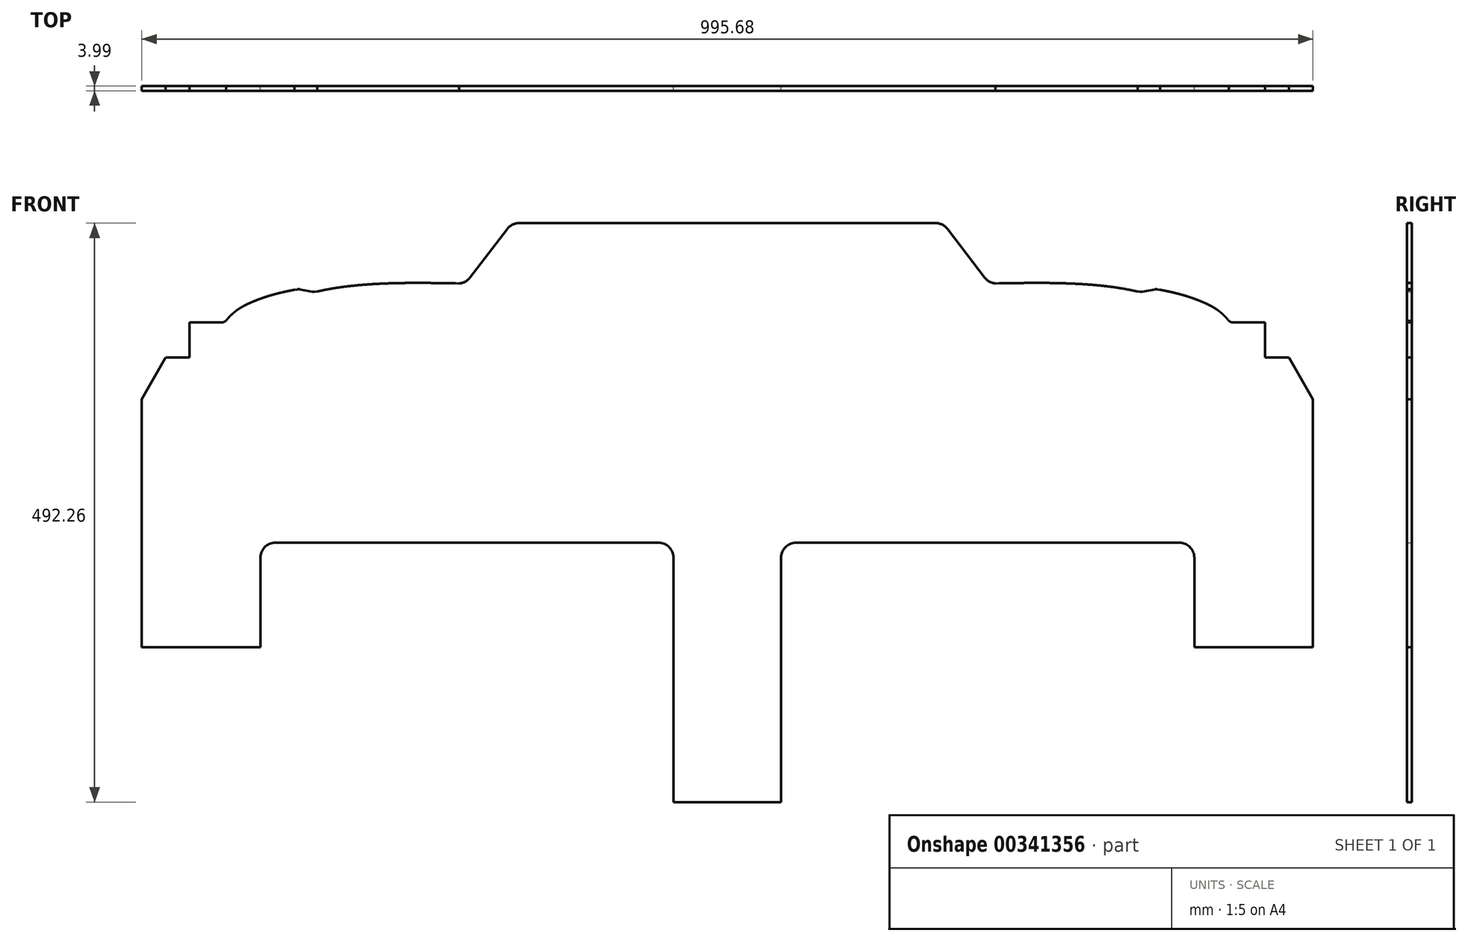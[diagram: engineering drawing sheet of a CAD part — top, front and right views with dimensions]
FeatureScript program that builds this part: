
annotation { "Feature Type Name" : "Feature", "Feature Type Description" : "" }
export const myFeature = defineFeature(function(context is Context, id is Id, definition is map)
    precondition{}
    {
        {
            var Q0;
            Q0=qCreatedBy(makeId("Front.planeOp"),FACE);
            var sketch = newSketch(context, id + "F0", { "sketchPlane" : qUnion([Q0])});
            skLineSegment(sketch, "E0", {"start": v(-497.84, 96.27) * mm, "end": v(-477.52, 131.83) * mm});
            skLineSegment(sketch, "E1", {"start": v(-477.52, 131.83) * mm, "end": v(-457.2, 131.83) * mm});
            skLineSegment(sketch, "E2", {"start": v(-457.2, 131.83) * mm, "end": v(-457.2, 161.67) * mm});
            skLineSegment(sketch, "E3", {"start": v(-457.2, 161.67) * mm, "end": v(-430.26, 161.67) * mm});
            skLineSegment(sketch, "E4", {"start": v(-187.2, 241.14) * mm, "end": v(-218.8, 199.83) * mm});
            skLineSegment(sketch, "E5", {"start": v(-367.96, 189.44) * mm, "end": v(-365.6, 189.83) * mm});
            skLineSegment(sketch, "E6", {"start": v(-363.38, 189.8) * mm, "end": v(-352.8, 187.74) * mm});
            skLineSegment(sketch, "E7", {"start": v(-350.76, 187.68) * mm, "end": v(-348.83, 187.94) * mm});
            skLineSegment(sketch, "E8", {"start": v(-397, -38.35) * mm, "end": v(-397, -114.55) * mm});
            skLineSegment(sketch, "E9", {"start": v(-177.11, 246.13) * mm, "end": v(0, 246.13) * mm});
            skArc(sketch, "E10", {"start": v(-344.04, 189) * mm, "mid": v(-346.44, 188.48) * mm, "end": v(-348.83, 187.94) * mm});
            skArc(sketch, "E11", {"start": v(-339.2, 189.94) * mm, "mid": v(-341.62, 189.48) * mm, "end": v(-344.04, 189) * mm});
            skArc(sketch, "E12", {"start": v(-334.3, 190.78) * mm, "mid": v(-336.75, 190.37) * mm, "end": v(-339.2, 189.94) * mm});
            skArc(sketch, "E13", {"start": v(-329.39, 191.53) * mm, "mid": v(-331.85, 191.17) * mm, "end": v(-334.3, 190.78) * mm});
            skArc(sketch, "E14", {"start": v(-324.46, 192.19) * mm, "mid": v(-326.92, 191.87) * mm, "end": v(-329.39, 191.53) * mm});
            skArc(sketch, "E15", {"start": v(-319.53, 192.77) * mm, "mid": v(-322, 192.49) * mm, "end": v(-324.46, 192.19) * mm});
            skArc(sketch, "E16", {"start": v(-314.6, 193.26) * mm, "mid": v(-317.07, 193.02) * mm, "end": v(-319.53, 192.77) * mm});
            skArc(sketch, "E17", {"start": v(-309.7, 193.7) * mm, "mid": v(-312.16, 193.49) * mm, "end": v(-314.6, 193.26) * mm});
            skArc(sketch, "E18", {"start": v(-304.85, 194.05) * mm, "mid": v(-307.28, 193.88) * mm, "end": v(-309.7, 193.7) * mm});
            skArc(sketch, "E19", {"start": v(-300.03, 194.36) * mm, "mid": v(-302.44, 194.21) * mm, "end": v(-304.85, 194.05) * mm});
            skArc(sketch, "E20", {"start": v(-295.28, 194.6) * mm, "mid": v(-297.66, 194.49) * mm, "end": v(-300.03, 194.36) * mm});
            skArc(sketch, "E21", {"start": v(-290.6, 194.8) * mm, "mid": v(-292.94, 194.71) * mm, "end": v(-295.28, 194.6) * mm});
            skArc(sketch, "E22", {"start": v(-286.01, 194.97) * mm, "mid": v(-288.3, 194.9) * mm, "end": v(-290.6, 194.8) * mm});
            skArc(sketch, "E23", {"start": v(-283.6, 195.04) * mm, "mid": v(-284.81, 195) * mm, "end": v(-286.01, 194.97) * mm});
            skArc(sketch, "E24", {"start": v(-281.23, 195.1) * mm, "mid": v(-282.42, 195.07) * mm, "end": v(-283.6, 195.04) * mm});
            skArc(sketch, "E25", {"start": v(-278.86, 195.15) * mm, "mid": v(-280.05, 195.13) * mm, "end": v(-281.23, 195.1) * mm});
            skArc(sketch, "E26", {"start": v(-276.5, 195.2) * mm, "mid": v(-277.68, 195.17) * mm, "end": v(-278.86, 195.15) * mm});
            skArc(sketch, "E27", {"start": v(-274.15, 195.23) * mm, "mid": v(-275.33, 195.21) * mm, "end": v(-276.5, 195.2) * mm});
            skArc(sketch, "E28", {"start": v(-271.79, 195.25) * mm, "mid": v(-272.97, 195.24) * mm, "end": v(-274.15, 195.23) * mm});
            skArc(sketch, "E29", {"start": v(-269.41, 195.27) * mm, "mid": v(-270.6, 195.26) * mm, "end": v(-271.79, 195.25) * mm});
            skArc(sketch, "E30", {"start": v(-267.02, 195.28) * mm, "mid": v(-268.22, 195.28) * mm, "end": v(-269.41, 195.27) * mm});
            skArc(sketch, "E31", {"start": v(-264.6, 195.29) * mm, "mid": v(-265.81, 195.29) * mm, "end": v(-267.02, 195.28) * mm});
            skArc(sketch, "E32", {"start": v(-262.16, 195.29) * mm, "mid": v(-263.38, 195.29) * mm, "end": v(-264.6, 195.29) * mm});
            skArc(sketch, "E33", {"start": v(-259.67, 195.28) * mm, "mid": v(-260.91, 195.28) * mm, "end": v(-262.16, 195.29) * mm});
            skArc(sketch, "E34", {"start": v(-257.14, 195.26) * mm, "mid": v(-258.4, 195.27) * mm, "end": v(-259.67, 195.28) * mm});
            skArc(sketch, "E35", {"start": v(-254.56, 195.24) * mm, "mid": v(-255.85, 195.25) * mm, "end": v(-257.14, 195.26) * mm});
            skArc(sketch, "E36", {"start": v(-251.92, 195.22) * mm, "mid": v(-253.24, 195.23) * mm, "end": v(-254.56, 195.24) * mm});
            skArc(sketch, "E37", {"start": v(-249.2, 195.19) * mm, "mid": v(-250.56, 195.2) * mm, "end": v(-251.92, 195.22) * mm});
            skArc(sketch, "E38", {"start": v(-246.43, 195.15) * mm, "mid": v(-247.82, 195.17) * mm, "end": v(-249.2, 195.19) * mm});
            skArc(sketch, "E39", {"start": v(-243.58, 195.12) * mm, "mid": v(-245, 195.14) * mm, "end": v(-246.43, 195.15) * mm});
            skArc(sketch, "E40", {"start": v(-240.64, 195.08) * mm, "mid": v(-242.1, 195.1) * mm, "end": v(-243.58, 195.12) * mm});
            skArc(sketch, "E41", {"start": v(-237.6, 195.03) * mm, "mid": v(-239.12, 195.05) * mm, "end": v(-240.64, 195.08) * mm});
            skArc(sketch, "E42", {"start": v(-234.48, 194.98) * mm, "mid": v(-236.04, 195) * mm, "end": v(-237.6, 195.03) * mm});
            skArc(sketch, "E43", {"start": v(-231.24, 194.93) * mm, "mid": v(-232.86, 194.96) * mm, "end": v(-234.48, 194.98) * mm});
            skArc(sketch, "E44", {"start": v(-227.9, 194.88) * mm, "mid": v(-229.57, 194.9) * mm, "end": v(-231.24, 194.93) * mm});
            skArc(sketch, "E45", {"start": v(-425.3, 164.29) * mm, "mid": v(-425.78, 163.69) * mm, "end": v(-426.27, 163.08) * mm});
            skArc(sketch, "E46", {"start": v(-424.3, 165.44) * mm, "mid": v(-424.8, 164.87) * mm, "end": v(-425.3, 164.29) * mm});
            skArc(sketch, "E47", {"start": v(-423.3, 166.52) * mm, "mid": v(-423.8, 165.98) * mm, "end": v(-424.3, 165.44) * mm});
            skArc(sketch, "E48", {"start": v(-422.29, 167.56) * mm, "mid": v(-422.8, 167.05) * mm, "end": v(-423.3, 166.52) * mm});
            skArc(sketch, "E49", {"start": v(-421.27, 168.54) * mm, "mid": v(-421.78, 168.05) * mm, "end": v(-422.29, 167.56) * mm});
            skArc(sketch, "E50", {"start": v(-420.24, 169.47) * mm, "mid": v(-420.76, 169) * mm, "end": v(-421.27, 168.54) * mm});
            skArc(sketch, "E51", {"start": v(-419.2, 170.35) * mm, "mid": v(-419.72, 169.91) * mm, "end": v(-420.24, 169.47) * mm});
            skArc(sketch, "E52", {"start": v(-418.14, 171.19) * mm, "mid": v(-418.67, 170.77) * mm, "end": v(-419.2, 170.35) * mm});
            skArc(sketch, "E53", {"start": v(-417.08, 171.98) * mm, "mid": v(-417.62, 171.59) * mm, "end": v(-418.14, 171.19) * mm});
            skArc(sketch, "E54", {"start": v(-416.02, 172.74) * mm, "mid": v(-416.55, 172.37) * mm, "end": v(-417.08, 171.98) * mm});
            skArc(sketch, "E55", {"start": v(-414.94, 173.46) * mm, "mid": v(-415.48, 173.1) * mm, "end": v(-416.02, 172.74) * mm});
            skArc(sketch, "E56", {"start": v(-413.85, 174.14) * mm, "mid": v(-414.4, 173.8) * mm, "end": v(-414.94, 173.46) * mm});
            skArc(sketch, "E57", {"start": v(-412.75, 174.8) * mm, "mid": v(-413.3, 174.47) * mm, "end": v(-413.85, 174.14) * mm});
            skArc(sketch, "E58", {"start": v(-411.65, 175.42) * mm, "mid": v(-412.2, 175.1) * mm, "end": v(-412.75, 174.8) * mm});
            skArc(sketch, "E59", {"start": v(-410.54, 176.01) * mm, "mid": v(-411.1, 175.72) * mm, "end": v(-411.65, 175.42) * mm});
            skArc(sketch, "E60", {"start": v(-409.42, 176.59) * mm, "mid": v(-409.98, 176.3) * mm, "end": v(-410.54, 176.01) * mm});
            skArc(sketch, "E61", {"start": v(-408.29, 177.14) * mm, "mid": v(-408.85, 176.86) * mm, "end": v(-409.42, 176.59) * mm});
            skArc(sketch, "E62", {"start": v(-407.15, 177.67) * mm, "mid": v(-407.72, 177.4) * mm, "end": v(-408.29, 177.14) * mm});
            skArc(sketch, "E63", {"start": v(-406, 178.19) * mm, "mid": v(-406.58, 177.93) * mm, "end": v(-407.15, 177.67) * mm});
            skArc(sketch, "E64", {"start": v(-404.86, 178.7) * mm, "mid": v(-405.43, 178.44) * mm, "end": v(-406, 178.19) * mm});
            skArc(sketch, "E65", {"start": v(-403.7, 179.18) * mm, "mid": v(-404.28, 178.94) * mm, "end": v(-404.86, 178.7) * mm});
            skArc(sketch, "E66", {"start": v(-402.37, 179.74) * mm, "mid": v(-403.03, 179.46) * mm, "end": v(-403.7, 179.18) * mm});
            skArc(sketch, "E67", {"start": v(-401.02, 180.28) * mm, "mid": v(-401.7, 180.01) * mm, "end": v(-402.37, 179.74) * mm});
            skArc(sketch, "E68", {"start": v(-399.66, 180.82) * mm, "mid": v(-400.34, 180.55) * mm, "end": v(-401.02, 180.28) * mm});
            skArc(sketch, "E69", {"start": v(-398.29, 181.34) * mm, "mid": v(-398.98, 181.08) * mm, "end": v(-399.66, 180.82) * mm});
            skArc(sketch, "E70", {"start": v(-396.9, 181.86) * mm, "mid": v(-397.6, 181.6) * mm, "end": v(-398.29, 181.34) * mm});
            skArc(sketch, "E71", {"start": v(-395.48, 182.36) * mm, "mid": v(-396.19, 182.11) * mm, "end": v(-396.9, 181.86) * mm});
            skArc(sketch, "E72", {"start": v(-394.04, 182.86) * mm, "mid": v(-394.76, 182.61) * mm, "end": v(-395.48, 182.36) * mm});
            skArc(sketch, "E73", {"start": v(-392.58, 183.35) * mm, "mid": v(-393.3, 183.1) * mm, "end": v(-394.04, 182.86) * mm});
            skArc(sketch, "E74", {"start": v(-391.08, 183.83) * mm, "mid": v(-391.83, 183.6) * mm, "end": v(-392.58, 183.35) * mm});
            skArc(sketch, "E75", {"start": v(-389.56, 184.3) * mm, "mid": v(-390.32, 184.07) * mm, "end": v(-391.08, 183.83) * mm});
            skArc(sketch, "E76", {"start": v(-388, 184.77) * mm, "mid": v(-388.78, 184.54) * mm, "end": v(-389.56, 184.3) * mm});
            skArc(sketch, "E77", {"start": v(-386.4, 185.23) * mm, "mid": v(-387.2, 185) * mm, "end": v(-388, 184.77) * mm});
            skArc(sketch, "E78", {"start": v(-384.78, 185.68) * mm, "mid": v(-385.6, 185.45) * mm, "end": v(-386.4, 185.23) * mm});
            skArc(sketch, "E79", {"start": v(-383.1, 186.12) * mm, "mid": v(-383.94, 185.9) * mm, "end": v(-384.78, 185.68) * mm});
            skArc(sketch, "E80", {"start": v(-381.39, 186.56) * mm, "mid": v(-382.24, 186.34) * mm, "end": v(-383.1, 186.12) * mm});
            skArc(sketch, "E81", {"start": v(-379.62, 186.99) * mm, "mid": v(-380.5, 186.77) * mm, "end": v(-381.39, 186.56) * mm});
            skArc(sketch, "E82", {"start": v(-377.81, 187.4) * mm, "mid": v(-378.72, 187.2) * mm, "end": v(-379.62, 186.99) * mm});
            skArc(sketch, "E83", {"start": v(-375.95, 187.83) * mm, "mid": v(-376.88, 187.62) * mm, "end": v(-377.81, 187.4) * mm});
            skArc(sketch, "E84", {"start": v(-374.04, 188.24) * mm, "mid": v(-375, 188.04) * mm, "end": v(-375.95, 187.83) * mm});
            skArc(sketch, "E85", {"start": v(-372.07, 188.65) * mm, "mid": v(-373.06, 188.44) * mm, "end": v(-374.04, 188.24) * mm});
            skArc(sketch, "E86", {"start": v(-370.04, 189.05) * mm, "mid": v(-371.06, 188.85) * mm, "end": v(-372.07, 188.65) * mm});
            skArc(sketch, "E87", {"start": v(-367.96, 189.44) * mm, "mid": v(-369, 189.25) * mm, "end": v(-370.04, 189.05) * mm});
            skArc(sketch, "E88", {"start": v(-384.3, -25.65) * mm, "mid": v(-393.28, -29.37) * mm, "end": v(-397, -38.35) * mm});
            skArc(sketch, "E89", {"start": v(-45.72, -38.35) * mm, "mid": v(-49.44, -29.37) * mm, "end": v(-58.42, -25.65) * mm});
            skArc(sketch, "E90", {"start": v(-430.26, 161.67) * mm, "mid": v(-428.14, 162.03) * mm, "end": v(-426.27, 163.08) * mm});
            skArc(sketch, "E91", {"start": v(-177.11, 246.13) * mm, "mid": v(-182.74, 244.81) * mm, "end": v(-187.2, 241.14) * mm});
            skArc(sketch, "E92", {"start": v(-227.9, 194.88) * mm, "mid": v(-222.83, 196.39) * mm, "end": v(-218.8, 199.83) * mm});
            skArc(sketch, "E93", {"start": v(-352.8, 187.74) * mm, "mid": v(-351.79, 187.63) * mm, "end": v(-350.76, 187.68) * mm});
            skArc(sketch, "E94", {"start": v(-363.38, 189.8) * mm, "mid": v(-364.5, 189.9) * mm, "end": v(-365.6, 189.83) * mm});
            skLineSegment(sketch, "E95", {"start": v(-497.84, -114.55) * mm, "end": v(-397, -114.55) * mm});
            skLineSegment(sketch, "E96", {"start": v(-45.72, -38.35) * mm, "end": v(-45.72, -246.13) * mm});
            skLineSegment(sketch, "E97", {"start": v(-497.84, -114.55) * mm, "end": v(-497.84, 96.27) * mm});
            skLineSegment(sketch, "E98", {"start": v(-45.72, -246.13) * mm, "end": v(0, -246.13) * mm});
            skLineSegment(sketch, "E99", {"start": v(-384.3, -25.65) * mm, "end": v(-58.42, -25.65) * mm});
            skLineSegment(sketch, "E100", {"start": v(0, 246.13) * mm, "end": v(0, -246.13) * mm, "construction": true});
            skLineSegment(sketch, "E101", {"start": v(0, 246.13) * mm, "end": v(0, 330.84) * mm, "construction": true});
            skArc(sketch, "E102.MirrorCS", {"start": v(418.14, 171.19) * mm, "mid": v(418.67, 170.77) * mm, "end": v(419.2, 170.35) * mm});
            skArc(sketch, "E103.MirrorCS", {"start": v(414.94, 173.46) * mm, "mid": v(415.48, 173.1) * mm, "end": v(416.02, 172.74) * mm});
            skArc(sketch, "E104.MirrorCS", {"start": v(425.3, 164.29) * mm, "mid": v(425.78, 163.69) * mm, "end": v(426.27, 163.08) * mm});
            skArc(sketch, "E105.MirrorCS", {"start": v(420.24, 169.47) * mm, "mid": v(420.76, 169) * mm, "end": v(421.27, 168.54) * mm});
            skArc(sketch, "E106.MirrorCS", {"start": v(278.86, 195.15) * mm, "mid": v(280.05, 195.13) * mm, "end": v(281.23, 195.1) * mm});
            skArc(sketch, "E107.MirrorCS", {"start": v(283.6, 195.04) * mm, "mid": v(284.81, 195) * mm, "end": v(286.01, 194.97) * mm});
            skArc(sketch, "E108.MirrorCS", {"start": v(276.5, 195.2) * mm, "mid": v(277.68, 195.17) * mm, "end": v(278.86, 195.15) * mm});
            skArc(sketch, "E109.MirrorCS", {"start": v(421.27, 168.54) * mm, "mid": v(421.78, 168.05) * mm, "end": v(422.29, 167.56) * mm});
            skArc(sketch, "E110.MirrorCS", {"start": v(423.3, 166.52) * mm, "mid": v(423.8, 165.98) * mm, "end": v(424.3, 165.44) * mm});
            skArc(sketch, "E111.MirrorCS", {"start": v(422.29, 167.56) * mm, "mid": v(422.8, 167.05) * mm, "end": v(423.3, 166.52) * mm});
            skArc(sketch, "E112.MirrorCS", {"start": v(274.15, 195.23) * mm, "mid": v(275.33, 195.21) * mm, "end": v(276.5, 195.2) * mm});
            skArc(sketch, "E113.MirrorCS", {"start": v(281.23, 195.1) * mm, "mid": v(282.42, 195.07) * mm, "end": v(283.6, 195.04) * mm});
            skArc(sketch, "E114.MirrorCS", {"start": v(408.29, 177.14) * mm, "mid": v(408.85, 176.86) * mm, "end": v(409.42, 176.59) * mm});
            skArc(sketch, "E115.MirrorCS", {"start": v(419.2, 170.35) * mm, "mid": v(419.72, 169.91) * mm, "end": v(420.24, 169.47) * mm});
            skArc(sketch, "E116.MirrorCS", {"start": v(417.08, 171.98) * mm, "mid": v(417.62, 171.59) * mm, "end": v(418.14, 171.19) * mm});
            skArc(sketch, "E117.MirrorCS", {"start": v(424.3, 165.44) * mm, "mid": v(424.8, 164.87) * mm, "end": v(425.3, 164.29) * mm});
            skArc(sketch, "E118.MirrorCS", {"start": v(416.02, 172.74) * mm, "mid": v(416.55, 172.37) * mm, "end": v(417.08, 171.98) * mm});
            skArc(sketch, "E119.MirrorCS", {"start": v(402.37, 179.74) * mm, "mid": v(403.03, 179.46) * mm, "end": v(403.7, 179.18) * mm});
            skArc(sketch, "E120.MirrorCS", {"start": v(412.75, 174.8) * mm, "mid": v(413.3, 174.47) * mm, "end": v(413.85, 174.14) * mm});
            skArc(sketch, "E121.MirrorCS", {"start": v(395.48, 182.36) * mm, "mid": v(396.19, 182.11) * mm, "end": v(396.9, 181.86) * mm});
            skArc(sketch, "E122.MirrorCS", {"start": v(388, 184.77) * mm, "mid": v(388.78, 184.54) * mm, "end": v(389.56, 184.3) * mm});
            skArc(sketch, "E123.MirrorCS", {"start": v(271.79, 195.25) * mm, "mid": v(272.97, 195.24) * mm, "end": v(274.15, 195.23) * mm});
            skArc(sketch, "E124.MirrorCS", {"start": v(396.9, 181.86) * mm, "mid": v(397.6, 181.6) * mm, "end": v(398.29, 181.34) * mm});
            skArc(sketch, "E125.MirrorCS", {"start": v(409.42, 176.59) * mm, "mid": v(409.98, 176.3) * mm, "end": v(410.54, 176.01) * mm});
            skArc(sketch, "E126.MirrorCS", {"start": v(404.86, 178.7) * mm, "mid": v(405.43, 178.44) * mm, "end": v(406, 178.19) * mm});
            skArc(sketch, "E127.MirrorCS", {"start": v(399.66, 180.82) * mm, "mid": v(400.34, 180.55) * mm, "end": v(401.02, 180.28) * mm});
            skArc(sketch, "E128.MirrorCS", {"start": v(269.41, 195.27) * mm, "mid": v(270.6, 195.26) * mm, "end": v(271.79, 195.25) * mm});
            skArc(sketch, "E129.MirrorCS", {"start": v(267.02, 195.28) * mm, "mid": v(268.22, 195.28) * mm, "end": v(269.41, 195.27) * mm});
            skArc(sketch, "E130.MirrorCS", {"start": v(264.6, 195.29) * mm, "mid": v(265.81, 195.29) * mm, "end": v(267.02, 195.28) * mm});
            skArc(sketch, "E131.MirrorCS", {"start": v(391.08, 183.83) * mm, "mid": v(391.83, 183.6) * mm, "end": v(392.58, 183.35) * mm});
            skArc(sketch, "E132.MirrorCS", {"start": v(379.62, 186.99) * mm, "mid": v(380.5, 186.77) * mm, "end": v(381.39, 186.56) * mm});
            skArc(sketch, "E133.MirrorCS", {"start": v(392.58, 183.35) * mm, "mid": v(393.3, 183.1) * mm, "end": v(394.04, 182.86) * mm});
            skLineSegment(sketch, "E134.MirrorCS", {"start": v(350.76, 187.68) * mm, "end": v(348.83, 187.94) * mm});
            skArc(sketch, "E135.MirrorCS", {"start": v(386.4, 185.23) * mm, "mid": v(387.2, 185) * mm, "end": v(388, 184.77) * mm});
            skArc(sketch, "E136.MirrorCS", {"start": v(406, 178.19) * mm, "mid": v(406.58, 177.93) * mm, "end": v(407.15, 177.67) * mm});
            skArc(sketch, "E137.MirrorCS", {"start": v(430.26, 161.67) * mm, "mid": v(428.14, 162.03) * mm, "end": v(426.27, 163.08) * mm});
            skArc(sketch, "E138.MirrorCS", {"start": v(370.04, 189.05) * mm, "mid": v(371.06, 188.85) * mm, "end": v(372.07, 188.65) * mm});
            skArc(sketch, "E139.MirrorCS", {"start": v(407.15, 177.67) * mm, "mid": v(407.72, 177.4) * mm, "end": v(408.29, 177.14) * mm});
            skArc(sketch, "E140.MirrorCS", {"start": v(374.04, 188.24) * mm, "mid": v(375, 188.04) * mm, "end": v(375.95, 187.83) * mm});
            skArc(sketch, "E141.MirrorCS", {"start": v(372.07, 188.65) * mm, "mid": v(373.06, 188.44) * mm, "end": v(374.04, 188.24) * mm});
            skArc(sketch, "E142.MirrorCS", {"start": v(398.29, 181.34) * mm, "mid": v(398.98, 181.08) * mm, "end": v(399.66, 180.82) * mm});
            skArc(sketch, "E143.MirrorCS", {"start": v(384.78, 185.68) * mm, "mid": v(385.6, 185.45) * mm, "end": v(386.4, 185.23) * mm});
            skArc(sketch, "E144.MirrorCS", {"start": v(394.04, 182.86) * mm, "mid": v(394.76, 182.61) * mm, "end": v(395.48, 182.36) * mm});
            skArc(sketch, "E145.MirrorCS", {"start": v(375.95, 187.83) * mm, "mid": v(376.88, 187.62) * mm, "end": v(377.81, 187.4) * mm});
            skArc(sketch, "E146.MirrorCS", {"start": v(262.16, 195.29) * mm, "mid": v(263.38, 195.29) * mm, "end": v(264.6, 195.29) * mm});
            skArc(sketch, "E147.MirrorCS", {"start": v(410.54, 176.01) * mm, "mid": v(411.1, 175.72) * mm, "end": v(411.65, 175.42) * mm});
            skArc(sketch, "E148.MirrorCS", {"start": v(403.7, 179.18) * mm, "mid": v(404.28, 178.94) * mm, "end": v(404.86, 178.7) * mm});
            skArc(sketch, "E149.MirrorCS", {"start": v(413.85, 174.14) * mm, "mid": v(414.4, 173.8) * mm, "end": v(414.94, 173.46) * mm});
            skArc(sketch, "E150.MirrorCS", {"start": v(377.81, 187.4) * mm, "mid": v(378.72, 187.2) * mm, "end": v(379.62, 186.99) * mm});
            skArc(sketch, "E151.MirrorCS", {"start": v(411.65, 175.42) * mm, "mid": v(412.2, 175.1) * mm, "end": v(412.75, 174.8) * mm});
            skArc(sketch, "E152.MirrorCS", {"start": v(401.02, 180.28) * mm, "mid": v(401.7, 180.01) * mm, "end": v(402.37, 179.74) * mm});
            skArc(sketch, "E153.MirrorCS", {"start": v(352.8, 187.74) * mm, "mid": v(351.79, 187.63) * mm, "end": v(350.76, 187.68) * mm});
            skArc(sketch, "E154.MirrorCS", {"start": v(383.1, 186.12) * mm, "mid": v(383.94, 185.9) * mm, "end": v(384.78, 185.68) * mm});
            skArc(sketch, "E155.MirrorCS", {"start": v(344.04, 189) * mm, "mid": v(346.44, 188.48) * mm, "end": v(348.83, 187.94) * mm});
            skLineSegment(sketch, "E156.MirrorCS", {"start": v(367.96, 189.44) * mm, "end": v(365.6, 189.83) * mm});
            skArc(sketch, "E157.MirrorCS", {"start": v(367.96, 189.44) * mm, "mid": v(369, 189.25) * mm, "end": v(370.04, 189.05) * mm});
            skArc(sketch, "E158.MirrorCS", {"start": v(389.56, 184.3) * mm, "mid": v(390.32, 184.07) * mm, "end": v(391.08, 183.83) * mm});
            skArc(sketch, "E159.MirrorCS", {"start": v(381.39, 186.56) * mm, "mid": v(382.24, 186.34) * mm, "end": v(383.1, 186.12) * mm});
            skArc(sketch, "E160.MirrorCS", {"start": v(254.56, 195.24) * mm, "mid": v(255.85, 195.25) * mm, "end": v(257.14, 195.26) * mm});
            skArc(sketch, "E161.MirrorCS", {"start": v(237.6, 195.03) * mm, "mid": v(239.12, 195.05) * mm, "end": v(240.64, 195.08) * mm});
            skArc(sketch, "E162.MirrorCS", {"start": v(259.67, 195.28) * mm, "mid": v(260.91, 195.28) * mm, "end": v(262.16, 195.29) * mm});
            skArc(sketch, "E163.MirrorCS", {"start": v(286.01, 194.97) * mm, "mid": v(288.3, 194.9) * mm, "end": v(290.6, 194.8) * mm});
            skArc(sketch, "E164.MirrorCS", {"start": v(240.64, 195.08) * mm, "mid": v(242.1, 195.1) * mm, "end": v(243.58, 195.12) * mm});
            skArc(sketch, "E165.MirrorCS", {"start": v(251.92, 195.22) * mm, "mid": v(253.24, 195.23) * mm, "end": v(254.56, 195.24) * mm});
            skArc(sketch, "E166.MirrorCS", {"start": v(319.53, 192.77) * mm, "mid": v(322, 192.49) * mm, "end": v(324.46, 192.19) * mm});
            skArc(sketch, "E167.MirrorCS", {"start": v(249.2, 195.19) * mm, "mid": v(250.56, 195.2) * mm, "end": v(251.92, 195.22) * mm});
            skArc(sketch, "E168.MirrorCS", {"start": v(227.9, 194.88) * mm, "mid": v(229.57, 194.9) * mm, "end": v(231.24, 194.93) * mm});
            skArc(sketch, "E169.MirrorCS", {"start": v(231.24, 194.93) * mm, "mid": v(232.86, 194.96) * mm, "end": v(234.48, 194.98) * mm});
            skArc(sketch, "E170.MirrorCS", {"start": v(314.6, 193.26) * mm, "mid": v(317.07, 193.02) * mm, "end": v(319.53, 192.77) * mm});
            skArc(sketch, "E171.MirrorCS", {"start": v(246.43, 195.15) * mm, "mid": v(247.82, 195.17) * mm, "end": v(249.2, 195.19) * mm});
            skArc(sketch, "E172.MirrorCS", {"start": v(243.58, 195.12) * mm, "mid": v(245, 195.14) * mm, "end": v(246.43, 195.15) * mm});
            skArc(sketch, "E173.MirrorCS", {"start": v(234.48, 194.98) * mm, "mid": v(236.04, 195) * mm, "end": v(237.6, 195.03) * mm});
            skArc(sketch, "E174.MirrorCS", {"start": v(363.38, 189.8) * mm, "mid": v(364.5, 189.9) * mm, "end": v(365.6, 189.83) * mm});
            skArc(sketch, "E175.MirrorCS", {"start": v(257.14, 195.26) * mm, "mid": v(258.4, 195.27) * mm, "end": v(259.67, 195.28) * mm});
            skArc(sketch, "E176.MirrorCS", {"start": v(177.11, 246.13) * mm, "mid": v(182.74, 244.81) * mm, "end": v(187.2, 241.14) * mm});
            skArc(sketch, "E177.MirrorCS", {"start": v(339.2, 189.94) * mm, "mid": v(341.62, 189.48) * mm, "end": v(344.04, 189) * mm});
            skArc(sketch, "E178.MirrorCS", {"start": v(309.7, 193.7) * mm, "mid": v(312.16, 193.49) * mm, "end": v(314.6, 193.26) * mm});
            skArc(sketch, "E179.MirrorCS", {"start": v(304.85, 194.05) * mm, "mid": v(307.28, 193.88) * mm, "end": v(309.7, 193.7) * mm});
            skArc(sketch, "E180.MirrorCS", {"start": v(295.28, 194.6) * mm, "mid": v(297.66, 194.49) * mm, "end": v(300.03, 194.36) * mm});
            skArc(sketch, "E181.MirrorCS", {"start": v(329.39, 191.53) * mm, "mid": v(331.85, 191.17) * mm, "end": v(334.3, 190.78) * mm});
            skArc(sketch, "E182.MirrorCS", {"start": v(334.3, 190.78) * mm, "mid": v(336.75, 190.37) * mm, "end": v(339.2, 189.94) * mm});
            skArc(sketch, "E183.MirrorCS", {"start": v(227.9, 194.88) * mm, "mid": v(222.83, 196.39) * mm, "end": v(218.8, 199.83) * mm});
            skLineSegment(sketch, "E184.MirrorCS", {"start": v(363.38, 189.8) * mm, "end": v(352.8, 187.74) * mm});
            skArc(sketch, "E185.MirrorCS", {"start": v(324.46, 192.19) * mm, "mid": v(326.92, 191.87) * mm, "end": v(329.39, 191.53) * mm});
            skArc(sketch, "E186.MirrorCS", {"start": v(290.6, 194.8) * mm, "mid": v(292.94, 194.71) * mm, "end": v(295.28, 194.6) * mm});
            skArc(sketch, "E187.MirrorCS", {"start": v(300.03, 194.36) * mm, "mid": v(302.44, 194.21) * mm, "end": v(304.85, 194.05) * mm});
            skLineSegment(sketch, "E188.MirrorCS", {"start": v(497.84, -114.55) * mm, "end": v(397, -114.55) * mm});
            skLineSegment(sketch, "E189.MirrorCS", {"start": v(397, -38.35) * mm, "end": v(397, -114.55) * mm});
            skLineSegment(sketch, "E190.MirrorCS", {"start": v(45.72, -38.35) * mm, "end": v(45.72, -246.13) * mm});
            skLineSegment(sketch, "E191.MirrorCS", {"start": v(457.2, 161.67) * mm, "end": v(430.26, 161.67) * mm});
            skLineSegment(sketch, "E192.MirrorCS", {"start": v(384.3, -25.65) * mm, "end": v(58.42, -25.65) * mm});
            skArc(sketch, "E193.MirrorCS", {"start": v(384.3, -25.65) * mm, "mid": v(393.28, -29.37) * mm, "end": v(397, -38.35) * mm});
            skLineSegment(sketch, "E194.MirrorCS", {"start": v(477.52, 131.83) * mm, "end": v(457.2, 131.83) * mm});
            skLineSegment(sketch, "E195.MirrorCS", {"start": v(187.2, 241.14) * mm, "end": v(218.8, 199.83) * mm});
            skLineSegment(sketch, "E196.MirrorCS", {"start": v(497.84, 96.27) * mm, "end": v(477.52, 131.83) * mm});
            skLineSegment(sketch, "E197.MirrorCS", {"start": v(457.2, 131.83) * mm, "end": v(457.2, 161.67) * mm});
            skArc(sketch, "E198.MirrorCS", {"start": v(45.72, -38.35) * mm, "mid": v(49.44, -29.37) * mm, "end": v(58.42, -25.65) * mm});
            skLineSegment(sketch, "E199.MirrorCS", {"start": v(497.84, -114.55) * mm, "end": v(497.84, 96.27) * mm});
            skLineSegment(sketch, "E200", {"start": v(0, 246.13) * mm, "end": v(177.11, 246.13) * mm});
            skLineSegment(sketch, "E201", {"start": v(0, -246.13) * mm, "end": v(45.72, -246.13) * mm});
            skSolve(sketch);
        }
        {
            var Q0;
            Q0 = qSketchRegion(id + "F0", true);
            extrude(context, id + "F1", {"entities" : qUnion([Q0]), "flatOperationType" : FlatOperationType.REMOVE, "offsetDistance" : 25.4 * mm, "depth" : 4 * mm, "domain" : OperationDomain.MODEL});
        }
    });
